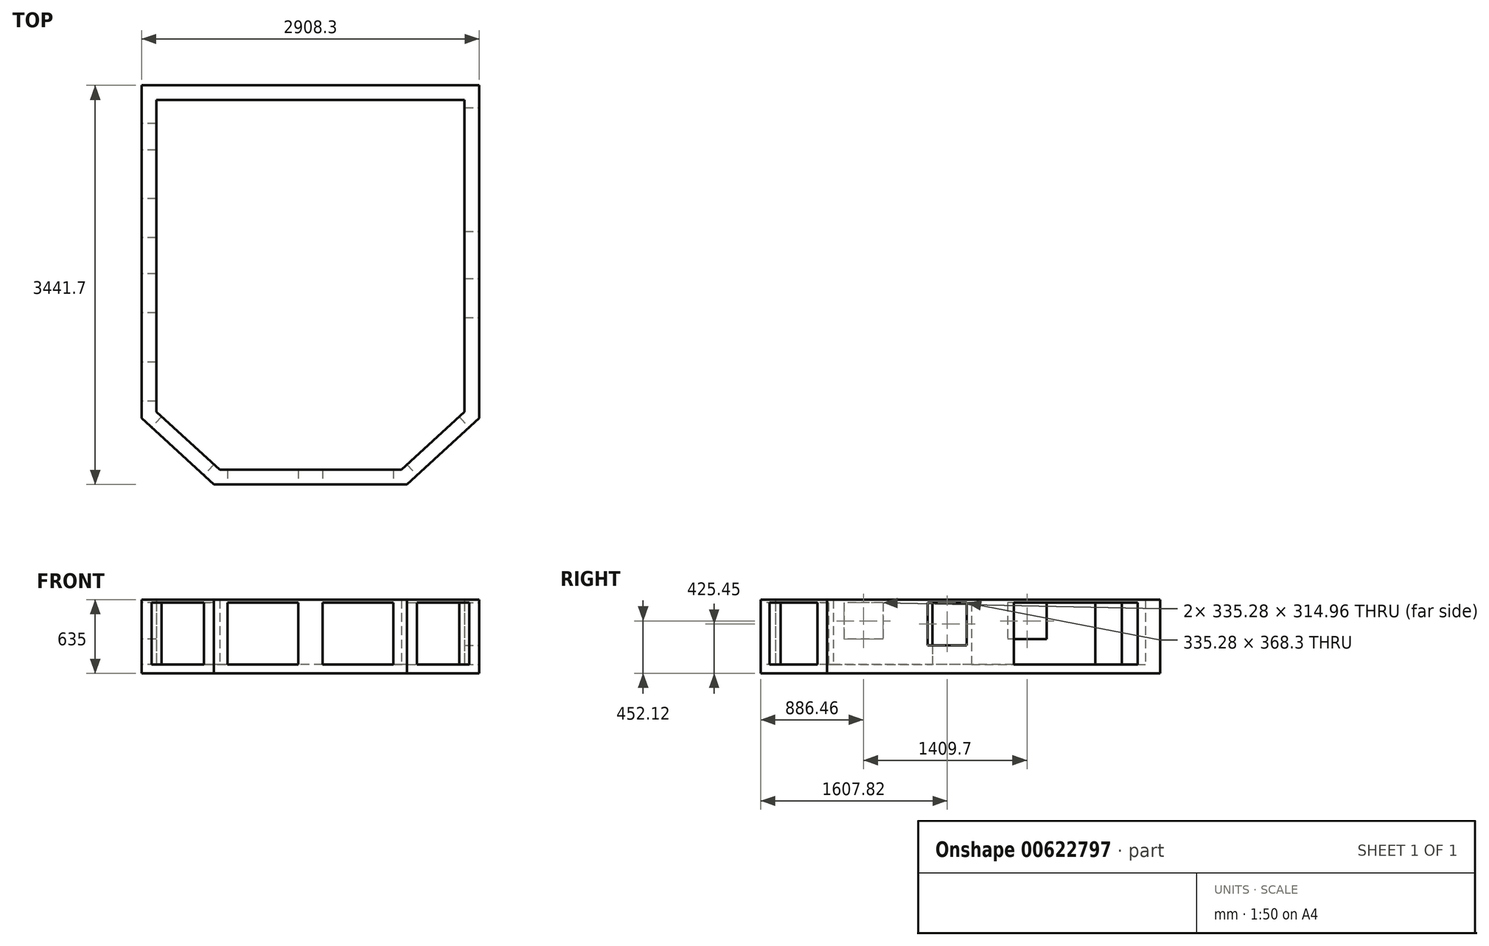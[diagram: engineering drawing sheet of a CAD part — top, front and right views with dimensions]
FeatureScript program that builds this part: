
annotation { "Feature Type Name" : "Feature", "Feature Type Description" : "" }
export const myFeature = defineFeature(function(context is Context, id is Id, definition is map)
    precondition{}
    {
        {
            var Q0;
            Q0=qCreatedBy(makeId("Top.planeOp"),FACE);
            var sketch = newSketch(context, id + "F0", { "sketchPlane" : qUnion([Q0])});
            skLineSegment(sketch, "E0", {"start": v(0, 0) * mm, "end": v(-2908.3, 0) * mm});
            skLineSegment(sketch, "E1", {"start": v(-2908.3, 0) * mm, "end": v(-2908.3, -2870.2) * mm});
            skLineSegment(sketch, "E2", {"start": v(-2908.3, -2870.2) * mm, "end": v(-2286, -3441.7) * mm});
            skLineSegment(sketch, "E3", {"start": v(-2286, -3441.7) * mm, "end": v(-622.3, -3441.7) * mm});
            skLineSegment(sketch, "E4", {"start": v(-622.3, -3441.7) * mm, "end": v(0, -2870.2) * mm});
            skLineSegment(sketch, "E5", {"start": v(0, -2870.2) * mm, "end": v(0, 0) * mm});
            skSolve(sketch);
        }
        {
            var Q0;
            Q0 = qSketchRegion(id + "F0", true);
            extrude(context, id + "F1", {"entities" : qUnion([Q0]), "oppositeDirection" : true, "depth" : 76.2 * mm, "offsetDistance" : 25.4 * mm});
        }
        {
            var Q0;
            Q0=makeQuery(id+"F1.opExtrude","CAP_FACE",FACE,{"disambiguationData":[OSD([sQuery(id+"F0.wireOp",EDGE,"E0"),sQuery(id+"F0.wireOp",EDGE,"E1"),sQuery(id+"F0.wireOp",EDGE,"E2"),sQuery(id+"F0.wireOp",EDGE,"E3"),sQuery(id+"F0.wireOp",EDGE,"E4"),sQuery(id+"F0.wireOp",EDGE,"E5")])],"isStart":false});
            var sketch = newSketch(context, id + "F2", { "sketchPlane" : qUnion([Q0])});
            skLineSegment(sketch, "E6", {"start": v(-2908.3, 0) * mm, "end": v(-2908.3, 2870.2) * mm});
            skLineSegment(sketch, "E7", {"start": v(-2908.3, 2870.2) * mm, "end": v(-2286, 3441.7) * mm});
            skLineSegment(sketch, "E8", {"start": v(-2286, 3441.7) * mm, "end": v(-622.3, 3441.7) * mm});
            skLineSegment(sketch, "E9", {"start": v(-622.3, 3441.7) * mm, "end": v(0, 2870.2) * mm});
            skLineSegment(sketch, "E10", {"start": v(0, 2870.2) * mm, "end": v(0, 0) * mm});
            skLineSegment(sketch, "E11", {"start": v(0, 0) * mm, "end": v(-2908.3, 0) * mm});
            skLineSegment(sketch, "E12.0", {"start": v(-127, 2814.4) * mm, "end": v(-127, 127) * mm});
            skLineSegment(sketch, "E12.1", {"start": v(-2781.3, 127) * mm, "end": v(-2781.3, 2814.4) * mm});
            skLineSegment(sketch, "E12.2", {"start": v(-2781.3, 2814.4) * mm, "end": v(-2236.53, 3314.7) * mm});
            skLineSegment(sketch, "E12.3", {"start": v(-127, 127) * mm, "end": v(-2781.3, 127) * mm});
            skLineSegment(sketch, "E12.4", {"start": v(-2236.53, 3314.7) * mm, "end": v(-671.77, 3314.7) * mm});
            skLineSegment(sketch, "E12.5", {"start": v(-671.77, 3314.7) * mm, "end": v(-127, 2814.4) * mm});
            skSolve(sketch);
        }
        {
            var Q0;
            Q0 = qSketchRegion(id + "F2", true);
            var Q1;
            Q1=makeQuery(id+"F2.imprint","IMPRINT",FACE,{"disambiguationData":[TD([[makeQuery(id+"F2.imprint","IMPRINT",EDGE,{"derivedFrom":sQuery(id+"F2.wireOp",EDGE,"E6")}),1.0]])]});
            extrude(context, id + "F3", {"entities" : qUnion([Q0, Q1]), "operationType" : NewBodyOperationType.ADD, "oppositeDirection" : true, "depth" : 635 * mm, "offsetDistance" : 25.4 * mm});
        }
        {
            var Q0;
            Q0=makeQuery(id+"F3.boolean.opBoolean","MERGE",FACE,{"derivedFrom":[makeQuery(id+"F1.opExtrude","SWEPT_FACE",FACE,{"disambiguationData":[OSD([sQuery(id+"F0.wireOp",EDGE,"E5")])]}),makeQuery(id+"F3.opExtrude","SWEPT_FACE",FACE,{"disambiguationData":[OSD([sQuery(id+"F2.wireOp",EDGE,"E10")])]})]});
            var sketch = newSketch(context, id + "F4", { "sketchPlane" : qUnion([Q0])});
            skLineSegment(sketch, "E13.bottom", {"start": v(-193.04, 533.4) * mm, "end": v(-1259.84, 533.4) * mm});
            skLineSegment(sketch, "E13.top", {"start": v(-193.04, 0) * mm, "end": v(-1259.84, 0) * mm});
            skLineSegment(sketch, "E13.left", {"start": v(-193.04, 533.4) * mm, "end": v(-193.04, 0) * mm});
            skLineSegment(sketch, "E13.right", {"start": v(-1259.84, 533.4) * mm, "end": v(-1259.84, 0) * mm});
            skLineSegment(sketch, "E14.bottom", {"start": v(-2001.52, 533.4) * mm, "end": v(-1666.24, 533.4) * mm});
            skLineSegment(sketch, "E14.top", {"start": v(-2001.52, 165.1) * mm, "end": v(-1666.24, 165.1) * mm});
            skLineSegment(sketch, "E14.left", {"start": v(-2001.52, 533.4) * mm, "end": v(-2001.52, 165.1) * mm});
            skLineSegment(sketch, "E14.right", {"start": v(-1666.24, 533.4) * mm, "end": v(-1666.24, 165.1) * mm});
            skSolve(sketch);
        }
        {
            var Q0;
            Q0 = qSketchRegion(id + "F4", true);
            var Q1;
            Q1=makeQuery(id+"F3.opExtrude","SWEPT_FACE",FACE,{"disambiguationData":[OSD([sQuery(id+"F2.wireOp",EDGE,"E12.0")])]});
            extrude(context, id + "F5", {"entities" : qUnion([Q0]), "operationType" : NewBodyOperationType.REMOVE, "endBound" : BoundingType.UP_TO_SURFACE, "oppositeDirection" : true, "depth" : 25.4 * mm, "endBoundEntityFace" : qUnion([Q1]), "offsetDistance" : 25.4 * mm});
        }
        {
            var Q0;
            Q0=makeQuery(id+"F3.boolean.opBoolean","MERGE",FACE,{"derivedFrom":[makeQuery(id+"F1.opExtrude","SWEPT_FACE",FACE,{"disambiguationData":[OSD([sQuery(id+"F0.wireOp",EDGE,"E4")])]}),makeQuery(id+"F3.opExtrude","SWEPT_FACE",FACE,{"disambiguationData":[OSD([sQuery(id+"F2.wireOp",EDGE,"E9")])]})]});
            var sketch = newSketch(context, id + "F6", { "sketchPlane" : qUnion([Q0])});
            skLineSegment(sketch, "E15.bottom", {"start": v(-2669.49, 533.4) * mm, "end": v(-2059.89, 533.4) * mm});
            skLineSegment(sketch, "E15.top", {"start": v(-2669.49, 0) * mm, "end": v(-2059.89, 0) * mm});
            skLineSegment(sketch, "E15.left", {"start": v(-2669.49, 533.4) * mm, "end": v(-2669.49, 0) * mm});
            skLineSegment(sketch, "E15.right", {"start": v(-2059.89, 533.4) * mm, "end": v(-2059.89, 0) * mm});
            skSolve(sketch);
        }
        {
            var Q0;
            Q0 = qSketchRegion(id + "F6", true);
            var Q1;
            Q1=makeQuery(id+"F3.opExtrude","SWEPT_FACE",FACE,{"disambiguationData":[OSD([sQuery(id+"F2.wireOp",EDGE,"E12.5")])]});
            extrude(context, id + "F7", {"entities" : qUnion([Q0]), "operationType" : NewBodyOperationType.REMOVE, "endBound" : BoundingType.UP_TO_SURFACE, "oppositeDirection" : true, "depth" : 25.4 * mm, "endBoundEntityFace" : qUnion([Q1]), "offsetDistance" : 25.4 * mm});
        }
        {
            var Q0;
            Q0=makeQuery(id+"F3.boolean.opBoolean","MERGE",FACE,{"derivedFrom":[makeQuery(id+"F1.opExtrude","SWEPT_FACE",FACE,{"disambiguationData":[OSD([sQuery(id+"F0.wireOp",EDGE,"E3")])]}),makeQuery(id+"F3.opExtrude","SWEPT_FACE",FACE,{"disambiguationData":[OSD([sQuery(id+"F2.wireOp",EDGE,"E8")])]})]});
            var sketch = newSketch(context, id + "F8", { "sketchPlane" : qUnion([Q0])});
            skLineSegment(sketch, "E16.bottom", {"start": v(-2169.16, 533.4) * mm, "end": v(-1559.56, 533.4) * mm});
            skLineSegment(sketch, "E16.top", {"start": v(-2169.16, 0) * mm, "end": v(-1559.56, 0) * mm});
            skLineSegment(sketch, "E16.left", {"start": v(-2169.16, 533.4) * mm, "end": v(-2169.16, 0) * mm});
            skLineSegment(sketch, "E16.right", {"start": v(-1559.56, 533.4) * mm, "end": v(-1559.56, 0) * mm});
            skLineSegment(sketch, "E17.bottom", {"start": v(-1348.74, 533.4) * mm, "end": v(-739.14, 533.4) * mm});
            skLineSegment(sketch, "E17.top", {"start": v(-1348.74, 0) * mm, "end": v(-739.14, 0) * mm});
            skLineSegment(sketch, "E17.left", {"start": v(-1348.74, 533.4) * mm, "end": v(-1348.74, 0) * mm});
            skLineSegment(sketch, "E17.right", {"start": v(-739.14, 533.4) * mm, "end": v(-739.14, 0) * mm});
            skSolve(sketch);
        }
        {
            var Q0;
            Q0 = qSketchRegion(id + "F8", true);
            var Q1;
            Q1=makeQuery(id+"F3.opExtrude","SWEPT_FACE",FACE,{"disambiguationData":[OSD([sQuery(id+"F2.wireOp",EDGE,"E12.4")])]});
            extrude(context, id + "F9", {"entities" : qUnion([Q0]), "operationType" : NewBodyOperationType.REMOVE, "endBound" : BoundingType.UP_TO_SURFACE, "oppositeDirection" : true, "depth" : 25.4 * mm, "endBoundEntityFace" : qUnion([Q1]), "offsetDistance" : 25.4 * mm});
        }
        {
            var Q0;
            Q0=makeQuery(id+"F3.boolean.opBoolean","MERGE",FACE,{"derivedFrom":[makeQuery(id+"F1.opExtrude","SWEPT_FACE",FACE,{"disambiguationData":[OSD([sQuery(id+"F0.wireOp",EDGE,"E2")])]}),makeQuery(id+"F3.opExtrude","SWEPT_FACE",FACE,{"disambiguationData":[OSD([sQuery(id+"F2.wireOp",EDGE,"E7")])]})]});
            var sketch = newSketch(context, id + "F10", { "sketchPlane" : qUnion([Q0])});
            skLineSegment(sketch, "E18.bottom", {"start": v(-83.8, 533.4) * mm, "end": v(525.8, 533.4) * mm});
            skLineSegment(sketch, "E18.top", {"start": v(-83.8, 0) * mm, "end": v(525.8, 0) * mm});
            skLineSegment(sketch, "E18.left", {"start": v(-83.8, 533.4) * mm, "end": v(-83.8, 0) * mm});
            skLineSegment(sketch, "E18.right", {"start": v(525.8, 533.4) * mm, "end": v(525.8, 0) * mm});
            skSolve(sketch);
        }
        {
            var Q0;
            Q0 = qSketchRegion(id + "F10", true);
            var Q1;
            Q1=makeQuery(id+"F3.opExtrude","SWEPT_FACE",FACE,{"disambiguationData":[OSD([sQuery(id+"F2.wireOp",EDGE,"E12.2")])]});
            extrude(context, id + "F11", {"entities" : qUnion([Q0]), "operationType" : NewBodyOperationType.REMOVE, "endBound" : BoundingType.UP_TO_SURFACE, "oppositeDirection" : true, "depth" : 25.4 * mm, "endBoundEntityFace" : qUnion([Q1]), "offsetDistance" : 25.4 * mm});
        }
        {
            var Q0;
            Q0=makeQuery(id+"F3.boolean.opBoolean","MERGE",FACE,{"derivedFrom":[makeQuery(id+"F1.opExtrude","SWEPT_FACE",FACE,{"disambiguationData":[OSD([sQuery(id+"F0.wireOp",EDGE,"E1")])]}),makeQuery(id+"F3.opExtrude","SWEPT_FACE",FACE,{"disambiguationData":[OSD([sQuery(id+"F2.wireOp",EDGE,"E6")])]})]});
            var sketch = newSketch(context, id + "F12", { "sketchPlane" : qUnion([Q0])});
            skLineSegment(sketch, "E19.bottom", {"start": v(330.2, 533.4) * mm, "end": v(558.8, 533.4) * mm});
            skLineSegment(sketch, "E19.top", {"start": v(330.2, 0) * mm, "end": v(558.8, 0) * mm});
            skLineSegment(sketch, "E19.left", {"start": v(330.2, 533.4) * mm, "end": v(330.2, 0) * mm});
            skLineSegment(sketch, "E19.right", {"start": v(558.8, 533.4) * mm, "end": v(558.8, 0) * mm});
            skLineSegment(sketch, "E20.bottom", {"start": v(977.9, 533.4) * mm, "end": v(1313.18, 533.4) * mm});
            skLineSegment(sketch, "E20.top", {"start": v(977.9, 218.44) * mm, "end": v(1313.18, 218.44) * mm});
            skLineSegment(sketch, "E20.left", {"start": v(977.9, 533.4) * mm, "end": v(977.9, 218.44) * mm});
            skLineSegment(sketch, "E20.right", {"start": v(1313.18, 533.4) * mm, "end": v(1313.18, 218.44) * mm});
            skLineSegment(sketch, "E21.bottom", {"start": v(1625.6, 533.4) * mm, "end": v(1960.88, 533.4) * mm});
            skLineSegment(sketch, "E21.top", {"start": v(1625.6, 0) * mm, "end": v(1960.88, 0) * mm});
            skLineSegment(sketch, "E21.left", {"start": v(1625.6, 533.4) * mm, "end": v(1625.6, 0) * mm});
            skLineSegment(sketch, "E21.right", {"start": v(1960.88, 533.4) * mm, "end": v(1960.88, 0) * mm});
            skLineSegment(sketch, "E22.bottom", {"start": v(2387.6, 533.4) * mm, "end": v(2722.88, 533.4) * mm});
            skLineSegment(sketch, "E22.top", {"start": v(2387.6, 218.44) * mm, "end": v(2722.88, 218.44) * mm});
            skLineSegment(sketch, "E22.left", {"start": v(2387.6, 533.4) * mm, "end": v(2387.6, 218.44) * mm});
            skLineSegment(sketch, "E22.right", {"start": v(2722.88, 533.4) * mm, "end": v(2722.88, 218.44) * mm});
            skSolve(sketch);
        }
        {
            var Q0;
            Q0 = qSketchRegion(id + "F12", true);
            var Q1;
            Q1=makeQuery(id+"F3.opExtrude","SWEPT_FACE",FACE,{"disambiguationData":[OSD([sQuery(id+"F2.wireOp",EDGE,"E12.1")])]});
            extrude(context, id + "F13", {"entities" : qUnion([Q0]), "operationType" : NewBodyOperationType.REMOVE, "endBound" : BoundingType.UP_TO_SURFACE, "oppositeDirection" : true, "depth" : 25.4 * mm, "endBoundEntityFace" : qUnion([Q1]), "offsetDistance" : 25.4 * mm});
        }
    });
